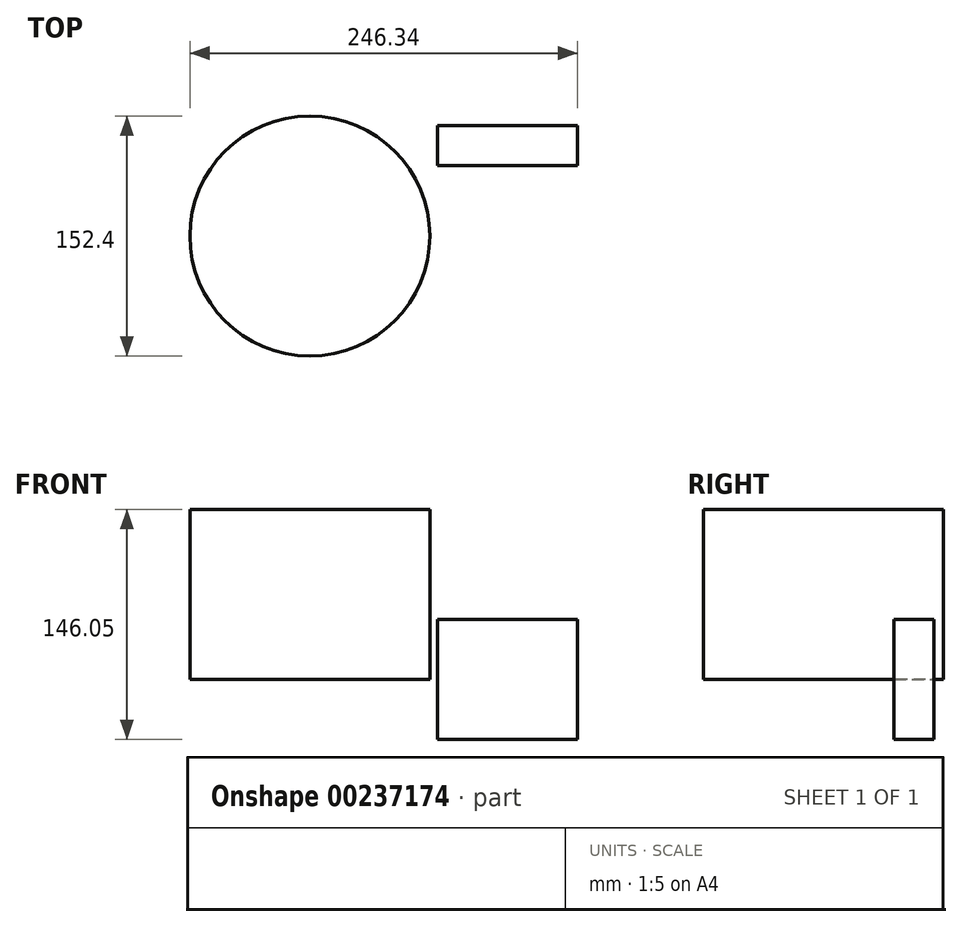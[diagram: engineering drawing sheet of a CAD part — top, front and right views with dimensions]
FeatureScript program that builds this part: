
annotation { "Feature Type Name" : "Feature", "Feature Type Description" : "" }
export const myFeature = defineFeature(function(context is Context, id is Id, definition is map)
    precondition{}
    {
        {
            var Q0;
            Q0=qCreatedBy(makeId("Top.planeOp"),FACE);
            var sketch = newSketch(context, id + "F0", { "sketchPlane" : qUnion([Q0])});
            skLineSegment(sketch, "E0.bottom", {"start": v(-44.45, -12.7) * mm, "end": v(44.45, -12.7) * mm});
            skLineSegment(sketch, "E0.top", {"start": v(-44.45, 12.7) * mm, "end": v(44.45, 12.7) * mm});
            skLineSegment(sketch, "E0.left", {"start": v(-44.45, -12.7) * mm, "end": v(-44.45, 12.7) * mm});
            skLineSegment(sketch, "E0.right", {"start": v(44.45, -12.7) * mm, "end": v(44.45, 12.7) * mm});
            skPoint(sketch, "E0.middle", {"position": v(0, 0) * mm});
            skSolve(sketch);
        }
        {
            var Q0;
            Q0 = qSketchRegion(id + "F0", true);
            extrude(context, id + "F1", {"entities" : qUnion([Q0]), "endBound" : BoundingType.SYMMETRIC, "depth" : 76.2 * mm});
        }
        {
            var Q0;
            Q0=qCreatedBy(makeId("Top.planeOp"),FACE);
            var sketch = newSketch(context, id + "F2", { "sketchPlane" : qUnion([Q0])});
            skCircle(sketch, "E1", {"center": v(-125.7, -57.35) * mm, "radius": 76.2 * mm});
            skSolve(sketch);
        }
        {
            var Q0;
            Q0 = qSketchRegion(id + "F2", true);
            extrude(context, id + "F3", {"entities" : qUnion([Q0]), "operationType" : NewBodyOperationType.ADD, "depth" : 107.95 * mm});
        }
    });
